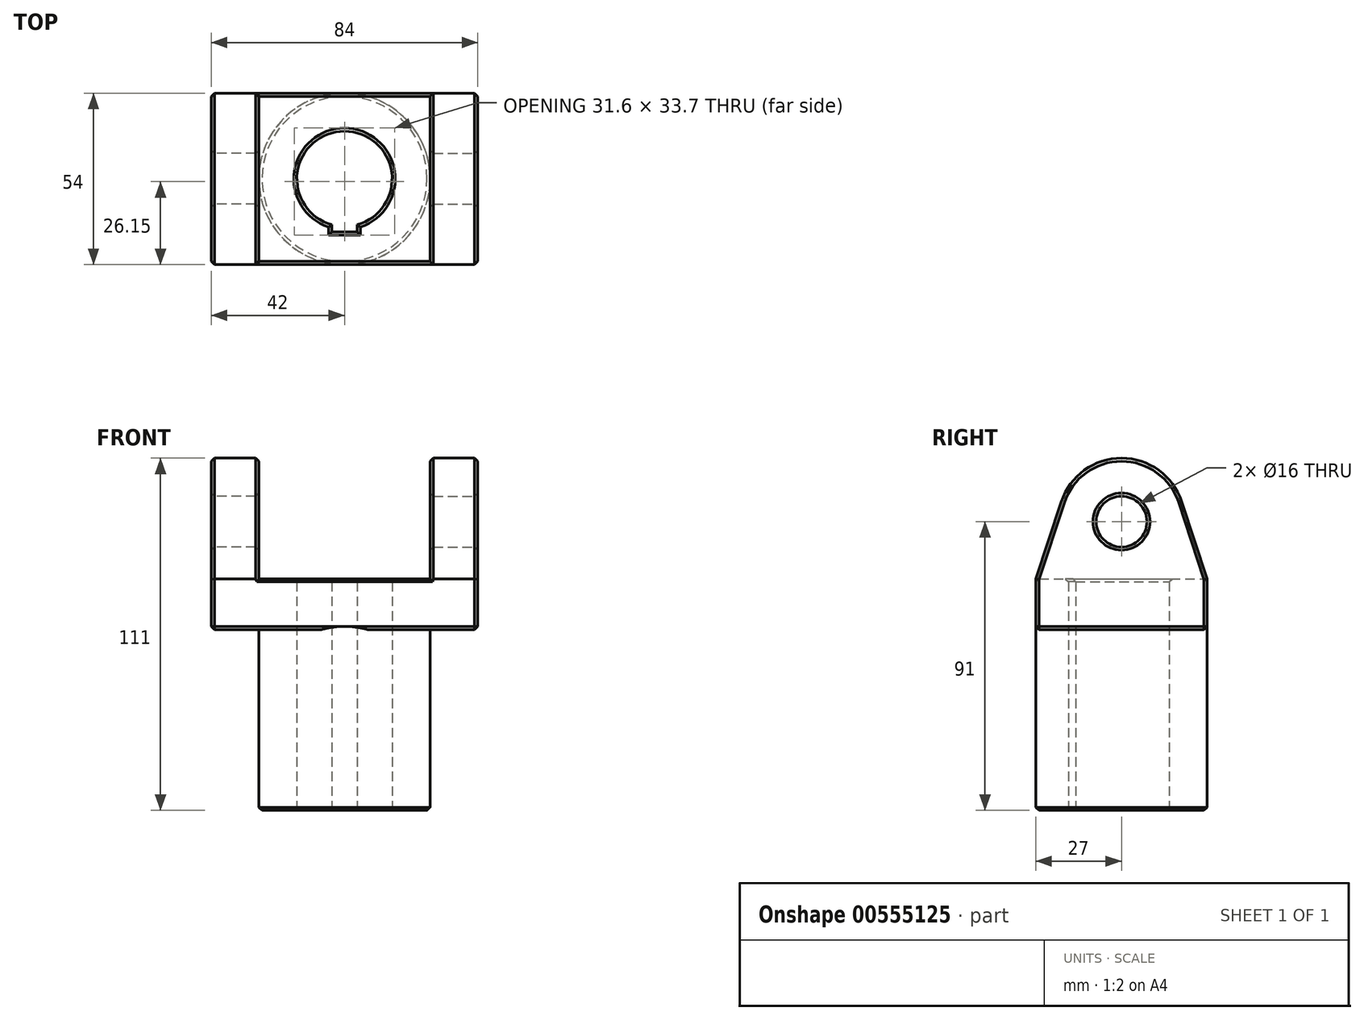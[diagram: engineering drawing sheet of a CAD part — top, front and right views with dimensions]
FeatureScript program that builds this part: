
annotation { "Feature Type Name" : "Feature", "Feature Type Description" : "" }
export const myFeature = defineFeature(function(context is Context, id is Id, definition is map)
    precondition{}
    {
        {
            var Q0;
            Q0=qCreatedBy(makeId("Top.planeOp"),FACE);
            var sketch = newSketch(context, id + "F0", { "sketchPlane" : qUnion([Q0])});
            skArc(sketch, "E0", {"start": v(4, -14.46) * mm, "mid": v(0, 15) * mm, "end": v(-4, -14.46) * mm});
            skCircle(sketch, "E1", {"center": v(0, 0) * mm, "radius": 27 * mm});
            skLineSegment(sketch, "E2.top", {"start": v(-4, -16.7) * mm, "end": v(4, -16.7) * mm});
            skLineSegment(sketch, "E2.left", {"start": v(-4, -14.46) * mm, "end": v(-4, -16.7) * mm});
            skLineSegment(sketch, "E2.right", {"start": v(4, -14.46) * mm, "end": v(4, -16.7) * mm});
            skPoint(sketch, "E3.orphan", {"position": v(-4, 0) * mm});
            skPoint(sketch, "E4.orphan", {"position": v(4, 0) * mm});
            skSolve(sketch);
        }
        {
            var Q0;
            Q0=makeQuery(id+"F0.imprint","IMPRINT",FACE,{"disambiguationData":[TD([[makeQuery(id+"F0.imprint","IMPRINT",EDGE,{"derivedFrom":sQuery(id+"F0.wireOp",EDGE,"E0")}),-1.0]])]});
            extrude(context, id + "F1", {"entities" : qUnion([Q0]), "depth" : 73 * mm, "offsetDistance" : 25 * mm});
        }
        {
            var Q0;
            Q0=makeQuery(id+"F1.opExtrude","CAP_FACE",FACE,{"disambiguationData":[OSD([sQuery(id+"F0.wireOp",EDGE,"E0"),sQuery(id+"F0.wireOp",EDGE,"E1"),sQuery(id+"F0.wireOp",EDGE,"E2.top"),sQuery(id+"F0.wireOp",EDGE,"E2.left"),sQuery(id+"F0.wireOp",EDGE,"E2.right")])],"isStart":false});
            var sketch = newSketch(context, id + "F2", { "sketchPlane" : qUnion([Q0])});
            skLineSegment(sketch, "E5.bottom", {"start": v(-42, 0) * mm, "end": v(42, 0) * mm});
            skLineSegment(sketch, "E5.top", {"start": v(-42, -27) * mm, "end": v(42, -27) * mm});
            skLineSegment(sketch, "E5.left", {"start": v(-42, 0) * mm, "end": v(-42, -27) * mm});
            skLineSegment(sketch, "E5.right", {"start": v(42, 0) * mm, "end": v(42, -27) * mm});
            skLineSegment(sketch, "E6.MirrorCS", {"start": v(-42, 27) * mm, "end": v(42, 27) * mm});
            skLineSegment(sketch, "E7.MirrorCS", {"start": v(42, 0) * mm, "end": v(42, 27) * mm});
            skLineSegment(sketch, "E8.MirrorCS", {"start": v(-42, 0) * mm, "end": v(-42, 27) * mm});
            skSolve(sketch);
        }
        {
            var Q0;
            {var subQ0=sQuery(id+"F2.wireOp",EDGE,"E8.MirrorCS");Q0=makeQuery(id+"F2.imprint","IMPRINT",FACE,{"disambiguationData":[TD([[makeQuery(id+"F2.imprint","IMPRINT",EDGE,{"derivedFrom":subQ0}),-1.0]])]});}
            var Q1;
            {var subQ0=sQuery(id+"F2.wireOp",EDGE,"E5.left");Q1=makeQuery(id+"F2.imprint","IMPRINT",FACE,{"disambiguationData":[TD([[makeQuery(id+"F2.imprint","IMPRINT",EDGE,{"derivedFrom":subQ0}),1.0]])]});}
            var Q2;
            {var subQ0=sQuery(id+"F2.wireOp",EDGE,"E7.MirrorCS");Q2=makeQuery(id+"F2.imprint","IMPRINT",FACE,{"disambiguationData":[TD([[makeQuery(id+"F2.imprint","IMPRINT",EDGE,{"derivedFrom":subQ0}),1.0]])]});}
            var Q3;
            {var subQ0=sQuery(id+"F2.wireOp",EDGE,"E5.right");Q3=makeQuery(id+"F2.imprint","IMPRINT",FACE,{"disambiguationData":[TD([[makeQuery(id+"F2.imprint","IMPRINT",EDGE,{"derivedFrom":subQ0}),-1.0]])]});}
            extrude(context, id + "F3", {"entities" : qUnion([Q0, Q1, Q2, Q3]), "operationType" : NewBodyOperationType.ADD, "oppositeDirection" : true, "depth" : 16 * mm, "offsetDistance" : 25 * mm});
        }
        {
            var Q0;
            Q0=makeQuery(id+"F3.opExtrude","SWEPT_FACE",FACE,{"disambiguationData":[OSD([sQuery(id+"F2.wireOp",EDGE,"E5.left"),sQuery(id+"F2.wireOp",EDGE,"E8.MirrorCS")])]});
            var sketch = newSketch(context, id + "F4", { "sketchPlane" : qUnion([Q0])});
            skArc(sketch, "E9", {"start": v(19, 97.27) * mm, "mid": v(0, 111) * mm, "end": v(-19, 97.27) * mm});
            skCircle(sketch, "E10", {"center": v(0, 91) * mm, "radius": 8 * mm});
            skLineSegment(sketch, "E11", {"start": v(-27, 73) * mm, "end": v(-19, 97.27) * mm});
            skLineSegment(sketch, "E12", {"start": v(27, 73) * mm, "end": v(19, 97.27) * mm});
            skPoint(sketch, "E13.start.orphan", {"position": v(0, 57) * mm});
            skLineSegment(sketch, "E14", {"start": v(-27, 73) * mm, "end": v(27, 73) * mm});
            skSolve(sketch);
        }
        {
            var Q0;
            Q0=makeQuery(id+"F4.imprint","IMPRINT",FACE,{"disambiguationData":[TD([[makeQuery(id+"F4.imprint","IMPRINT",EDGE,{"derivedFrom":sQuery(id+"F4.wireOp",EDGE,"E9")}),1.0]])]});
            extrude(context, id + "F5", {"entities" : qUnion([Q0]), "operationType" : NewBodyOperationType.ADD, "oppositeDirection" : true, "depth" : 15 * mm, "offsetDistance" : 25 * mm});
        }
        {
            var Q0;
            Q0=makeQuery(id+"F1.opExtrude","SWEPT_BODY",BODY,{"disambiguationData":[OSD([sQuery(id+"F0.wireOp",EDGE,"E0"),sQuery(id+"F0.wireOp",EDGE,"E1"),sQuery(id+"F0.wireOp",EDGE,"E2.top"),sQuery(id+"F0.wireOp",EDGE,"E2.left"),sQuery(id+"F0.wireOp",EDGE,"E2.right")])]});
            var Q1;
            Q1=qCreatedBy(makeId("Right.planeOp"),FACE);
            mirror(context, id + "F6", {"operationType" : NewBodyOperationType.ADD, "entities" : qUnion([Q0]), "mirrorPlane" : qUnion([Q1])});
        }
        {
            var Q0;
            Q0=makeQuery(id+"F1.opExtrude","CAP_EDGE",EDGE,{"disambiguationData":[OSD([sQuery(id+"F0.wireOp",EDGE,"E0")])],"isStart":false});
            var Q1;
            Q1=makeQuery(id+"F1.opExtrude","CAP_EDGE",EDGE,{"disambiguationData":[OSD([sQuery(id+"F0.wireOp",EDGE,"E2.top")])],"isStart":false});
            var Q2;
            Q2=makeQuery(id+"F1.opExtrude","CAP_EDGE",EDGE,{"disambiguationData":[OSD([sQuery(id+"F0.wireOp",EDGE,"E2.left")])],"isStart":false});
            var Q3;
            Q3=makeQuery(id+"F1.opExtrude","CAP_EDGE",EDGE,{"disambiguationData":[OSD([sQuery(id+"F0.wireOp",EDGE,"E2.right")])],"isStart":false});
            chamfer(context, id + "F7", {"entities" : qUnion([Q0, Q1, Q2, Q3]), "width" : 1 * mm, "tangentPropagation" : true});
        }
        {
            var Q0;
            Q0=makeQuery(id+"F1.opExtrude","CAP_EDGE",EDGE,{"disambiguationData":[OSD([sQuery(id+"F0.wireOp",EDGE,"E1")])],"isStart":true});
            var Q1;
            Q1=makeQuery(id+"F1.opExtrude","CAP_EDGE",EDGE,{"disambiguationData":[OSD([sQuery(id+"F0.wireOp",EDGE,"E0")])],"isStart":true});
            var Q2;
            Q2=makeQuery(id+"F1.opExtrude","CAP_EDGE",EDGE,{"disambiguationData":[OSD([sQuery(id+"F0.wireOp",EDGE,"E2.top")])],"isStart":true});
            var Q3;
            Q3=makeQuery(id+"F1.opExtrude","CAP_EDGE",EDGE,{"disambiguationData":[OSD([sQuery(id+"F0.wireOp",EDGE,"E2.left")])],"isStart":true});
            var Q4;
            Q4=makeQuery(id+"F1.opExtrude","CAP_EDGE",EDGE,{"disambiguationData":[OSD([sQuery(id+"F0.wireOp",EDGE,"E2.right")])],"isStart":true});
            chamfer(context, id + "F8", {"entities" : qUnion([Q0, Q1, Q2, Q3, Q4]), "width" : 1 * mm, "tangentPropagation" : true});
        }
        {
            var Q0;
            {var subQ0=sQuery(id+"F2.wireOp",EDGE,"E5.top");Q0=makeQuery(id+"F3.opExtrude","CAP_EDGE",EDGE,{"disambiguationData":[OSD([subQ0]),TDD([makeQuery(id+"F2.imprint","IMPRINT",EDGE,{"disambiguationData":[TD([[makeQuery(id+"F2.imprint","INTERSECT",VERTEX,{"derivedFrom":[subQ0,sQuery(id+"F2.wireOp",EDGE,"E5.left")]}),-1.0]])],"derivedFrom":subQ0})])],"isStart":false});}
            var Q1;
            {var subQ0=sQuery(id+"F2.wireOp",EDGE,"E6.MirrorCS");Q1=makeQuery(id+"F3.opExtrude","CAP_EDGE",EDGE,{"disambiguationData":[OSD([subQ0]),TDD([makeQuery(id+"F2.imprint","IMPRINT",EDGE,{"disambiguationData":[TD([[makeQuery(id+"F2.imprint","INTERSECT",VERTEX,{"derivedFrom":[subQ0,sQuery(id+"F2.wireOp",EDGE,"E8.MirrorCS")]}),-1.0]])],"derivedFrom":subQ0})])],"isStart":false});}
            var Q2;
            Q2=makeQuery(id+"F3.opExtrude","CAP_EDGE",EDGE,{"disambiguationData":[OSD([sQuery(id+"F2.wireOp",EDGE,"E5.right"),sQuery(id+"F2.wireOp",EDGE,"E7.MirrorCS")])],"isStart":false});
            var Q3;
            Q3=makeQuery(id+"F3.opExtrude","CAP_EDGE",EDGE,{"disambiguationData":[OSD([sQuery(id+"F2.wireOp",EDGE,"E5.left"),sQuery(id+"F2.wireOp",EDGE,"E8.MirrorCS")])],"isStart":false});
            var Q4;
            Q4=makeQuery(id+"F6.opPattern","COPY",EDGE,{"derivedFrom":makeQuery(id+"F5.opExtrude","CAP_EDGE",EDGE,{"disambiguationData":[OSD([sQuery(id+"F4.wireOp",EDGE,"E9")])],"isStart":false}),"instanceName":"1"});
            var Q5;
            Q5=makeQuery(id+"F5.boolean.opBoolean","MERGE",FACE,{"derivedFrom":[makeQuery(id+"F3.opExtrude","SWEPT_FACE",FACE,{"disambiguationData":[OSD([sQuery(id+"F2.wireOp",EDGE,"E5.left"),sQuery(id+"F2.wireOp",EDGE,"E8.MirrorCS")])]}),makeQuery(id+"F5.opExtrude","CAP_FACE",FACE,{"disambiguationData":[OSD([sQuery(id+"F4.wireOp",EDGE,"E9"),sQuery(id+"F4.wireOp",EDGE,"E10"),sQuery(id+"F4.wireOp",EDGE,"E11"),sQuery(id+"F4.wireOp",EDGE,"E12"),sQuery(id+"F4.wireOp",EDGE,"E14")])],"isStart":true})]});
            var Q6;
            Q6=makeQuery(id+"F5.opExtrude","CAP_EDGE",EDGE,{"disambiguationData":[OSD([sQuery(id+"F4.wireOp",EDGE,"E9")])],"isStart":false});
            var Q7;
            Q7=makeQuery(id+"F6.boolean.opBoolean","MERGE",FACE,{"derivedFrom":[makeQuery(id+"F3.opExtrude","SWEPT_FACE",FACE,{"disambiguationData":[OSD([sQuery(id+"F2.wireOp",EDGE,"E5.right"),sQuery(id+"F2.wireOp",EDGE,"E7.MirrorCS")])]}),makeQuery(id+"F6.opPattern","COPY",FACE,{"derivedFrom":makeQuery(id+"F5.boolean.opBoolean","MERGE",FACE,{"derivedFrom":[makeQuery(id+"F3.opExtrude","SWEPT_FACE",FACE,{"disambiguationData":[OSD([sQuery(id+"F2.wireOp",EDGE,"E5.left"),sQuery(id+"F2.wireOp",EDGE,"E8.MirrorCS")])]}),makeQuery(id+"F5.opExtrude","CAP_FACE",FACE,{"disambiguationData":[OSD([sQuery(id+"F4.wireOp",EDGE,"E9"),sQuery(id+"F4.wireOp",EDGE,"E10"),sQuery(id+"F4.wireOp",EDGE,"E11"),sQuery(id+"F4.wireOp",EDGE,"E12"),sQuery(id+"F4.wireOp",EDGE,"E14")])],"isStart":true})]}),"instanceName":"1"})]});
            chamfer(context, id + "F9", {"entities" : qUnion([Q0, Q1, Q2, Q3, Q4, Q5, Q6, Q7]), "width" : 1 * mm, "tangentPropagation" : true});
        }
        {
            var Q0;
            {var subQ0=sQuery(id+"F2.wireOp",EDGE,"E6.MirrorCS");var subQ2=sQuery(id+"F2.wireOp",EDGE,"E8.MirrorCS");var subQ3=makeQuery(id+"F3.boolean.opBoolean","MERGE",EDGE,{"derivedFrom":[makeQuery(id+"F3.opExtrude","CAP_EDGE",EDGE,{"disambiguationData":[OSD([subQ0]),TDD([makeQuery(id+"F2.imprint","IMPRINT",EDGE,{"disambiguationData":[TD([[makeQuery(id+"F2.imprint","INTERSECT",VERTEX,{"derivedFrom":[subQ0,subQ2]}),-1.0]])],"derivedFrom":subQ0})])],"isStart":true}),makeQuery(id+"F3.opExtrude","CAP_EDGE",EDGE,{"disambiguationData":[OSD([subQ0]),TDD([makeQuery(id+"F2.imprint","IMPRINT",EDGE,{"disambiguationData":[TD([[makeQuery(id+"F2.imprint","INTERSECT",VERTEX,{"derivedFrom":[subQ0,sQuery(id+"F2.wireOp",EDGE,"E7.MirrorCS")]}),1.0]])],"derivedFrom":subQ0})])],"isStart":true})]});var subQ4=makeQuery(id+"F5.boolean.opBoolean","SPLIT",EDGE,{"derivedFrom":subQ3});var subQ5=makeQuery(id+"F5.boolean.opBoolean","MERGE",EDGE,{"derivedFrom":[subQ3,makeQuery(id+"F5.opExtrude","SWEPT_EDGE",EDGE,{"disambiguationData":[OSD([subQ0,subQ2,sQuery(id+"F4.wireOp",EDGE,"E11"),sQuery(id+"F4.wireOp",EDGE,"E14")])]})]});Q0=makeQuery(id+"F9.opChamfer","MERGE",EDGE,{"derivedFrom":[subQ5,makeQuery(id+"F6.boolean.opBoolean","MERGE",EDGE,{"derivedFrom":[subQ4,makeQuery(id+"F6.opPattern","COPY",EDGE,{"derivedFrom":subQ5,"instanceName":"1"})]}),makeQuery(id+"F6.boolean.opBoolean","SPLIT",EDGE,{"derivedFrom":subQ4})]});}
            var Q1;
            {var subQ0=sQuery(id+"F2.wireOp",EDGE,"E5.top");var subQ2=sQuery(id+"F2.wireOp",EDGE,"E5.left");var subQ3=makeQuery(id+"F3.boolean.opBoolean","MERGE",EDGE,{"derivedFrom":[makeQuery(id+"F3.opExtrude","CAP_EDGE",EDGE,{"disambiguationData":[OSD([subQ0]),TDD([makeQuery(id+"F2.imprint","IMPRINT",EDGE,{"disambiguationData":[TD([[makeQuery(id+"F2.imprint","INTERSECT",VERTEX,{"derivedFrom":[subQ0,subQ2]}),-1.0]])],"derivedFrom":subQ0})])],"isStart":true}),makeQuery(id+"F3.opExtrude","CAP_EDGE",EDGE,{"disambiguationData":[OSD([subQ0]),TDD([makeQuery(id+"F2.imprint","IMPRINT",EDGE,{"disambiguationData":[TD([[makeQuery(id+"F2.imprint","INTERSECT",VERTEX,{"derivedFrom":[subQ0,sQuery(id+"F2.wireOp",EDGE,"E5.right")]}),1.0]])],"derivedFrom":subQ0})])],"isStart":true})]});var subQ4=makeQuery(id+"F5.boolean.opBoolean","SPLIT",EDGE,{"derivedFrom":subQ3});var subQ5=makeQuery(id+"F5.boolean.opBoolean","MERGE",EDGE,{"derivedFrom":[subQ3,makeQuery(id+"F5.opExtrude","SWEPT_EDGE",EDGE,{"disambiguationData":[OSD([subQ0,subQ2,sQuery(id+"F4.wireOp",EDGE,"E12"),sQuery(id+"F4.wireOp",EDGE,"E14")])]})]});Q1=makeQuery(id+"F9.opChamfer","MERGE",EDGE,{"derivedFrom":[subQ5,makeQuery(id+"F6.boolean.opBoolean","MERGE",EDGE,{"derivedFrom":[subQ4,makeQuery(id+"F6.opPattern","COPY",EDGE,{"derivedFrom":subQ5,"instanceName":"1"})]}),makeQuery(id+"F6.boolean.opBoolean","SPLIT",EDGE,{"derivedFrom":subQ4})]});}
            var Q2;
            Q2=makeQuery(id+"F6.opPattern","COPY",EDGE,{"derivedFrom":makeQuery(id+"F5.opExtrude","CAP_EDGE",EDGE,{"disambiguationData":[OSD([sQuery(id+"F4.wireOp",EDGE,"E10")])],"isStart":false}),"instanceName":"1"});
            var Q3;
            Q3=makeQuery(id+"F5.opExtrude","CAP_EDGE",EDGE,{"disambiguationData":[OSD([sQuery(id+"F4.wireOp",EDGE,"E10")])],"isStart":false});
            chamfer(context, id + "F10", {"entities" : qUnion([Q0, Q1, Q2, Q3]), "width" : 1 * mm, "tangentPropagation" : true});
        }
    });
